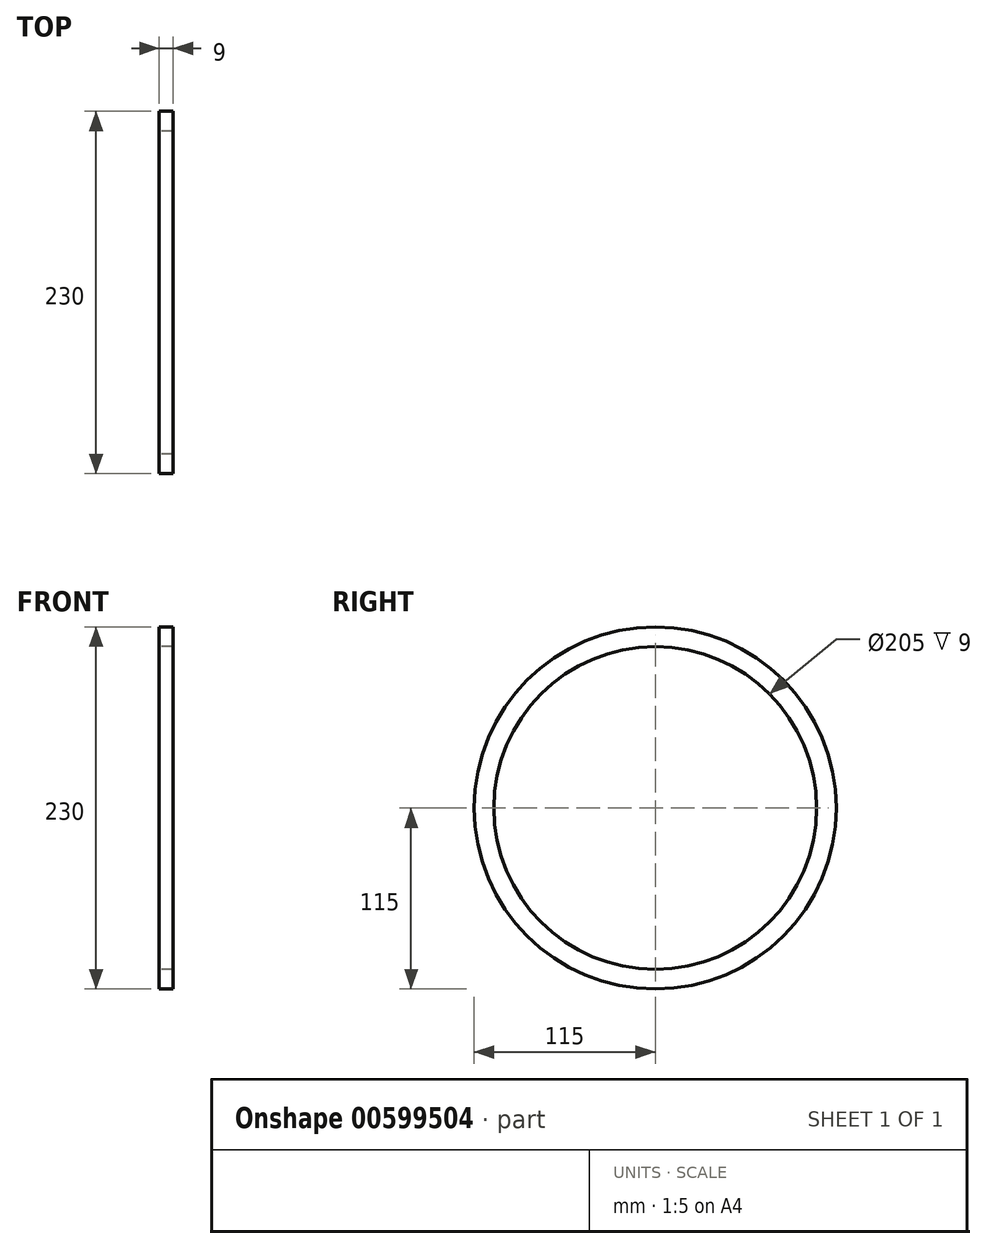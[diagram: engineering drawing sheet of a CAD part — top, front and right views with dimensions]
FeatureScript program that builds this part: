
annotation { "Feature Type Name" : "Feature", "Feature Type Description" : "" }
export const myFeature = defineFeature(function(context is Context, id is Id, definition is map)
    precondition{}
    {
        {
            var Q0;
            Q0=qCreatedBy(makeId("Front.planeOp"),FACE);
            var sketch = newSketch(context, id + "F0", { "sketchPlane" : qUnion([Q0])});
            skLineSegment(sketch, "E0", {"start": v(0, 108.75) * mm, "end": v(0, 0) * mm, "construction": true});
            skLineSegment(sketch, "E1", {"start": v(0, 0) * mm, "end": v(59.5, 0) * mm, "construction": true});
            skLineSegment(sketch, "E2.bottom", {"start": v(-4.5, 115) * mm, "end": v(4.5, 115) * mm});
            skLineSegment(sketch, "E2.top", {"start": v(-4.5, 102.5) * mm, "end": v(4.5, 102.5) * mm});
            skLineSegment(sketch, "E2.left", {"start": v(-4.5, 115) * mm, "end": v(-4.5, 102.5) * mm});
            skLineSegment(sketch, "E2.right", {"start": v(4.5, 115) * mm, "end": v(4.5, 102.5) * mm});
            skPoint(sketch, "E2.middle", {"position": v(0, 108.75) * mm});
            skSolve(sketch);
        }
        {
            var Q0;
            Q0 = qSketchRegion(id + "F0", true);
            var Q1;
            Q1=sQuery(id+"F0.wireOp",EDGE,"E1");
            revolve(context, id + "F1", {"entities" : qUnion([Q0]), "axis" : qUnion([Q1]), "revolveType" : RevolveType.FULL});
        }
    });
